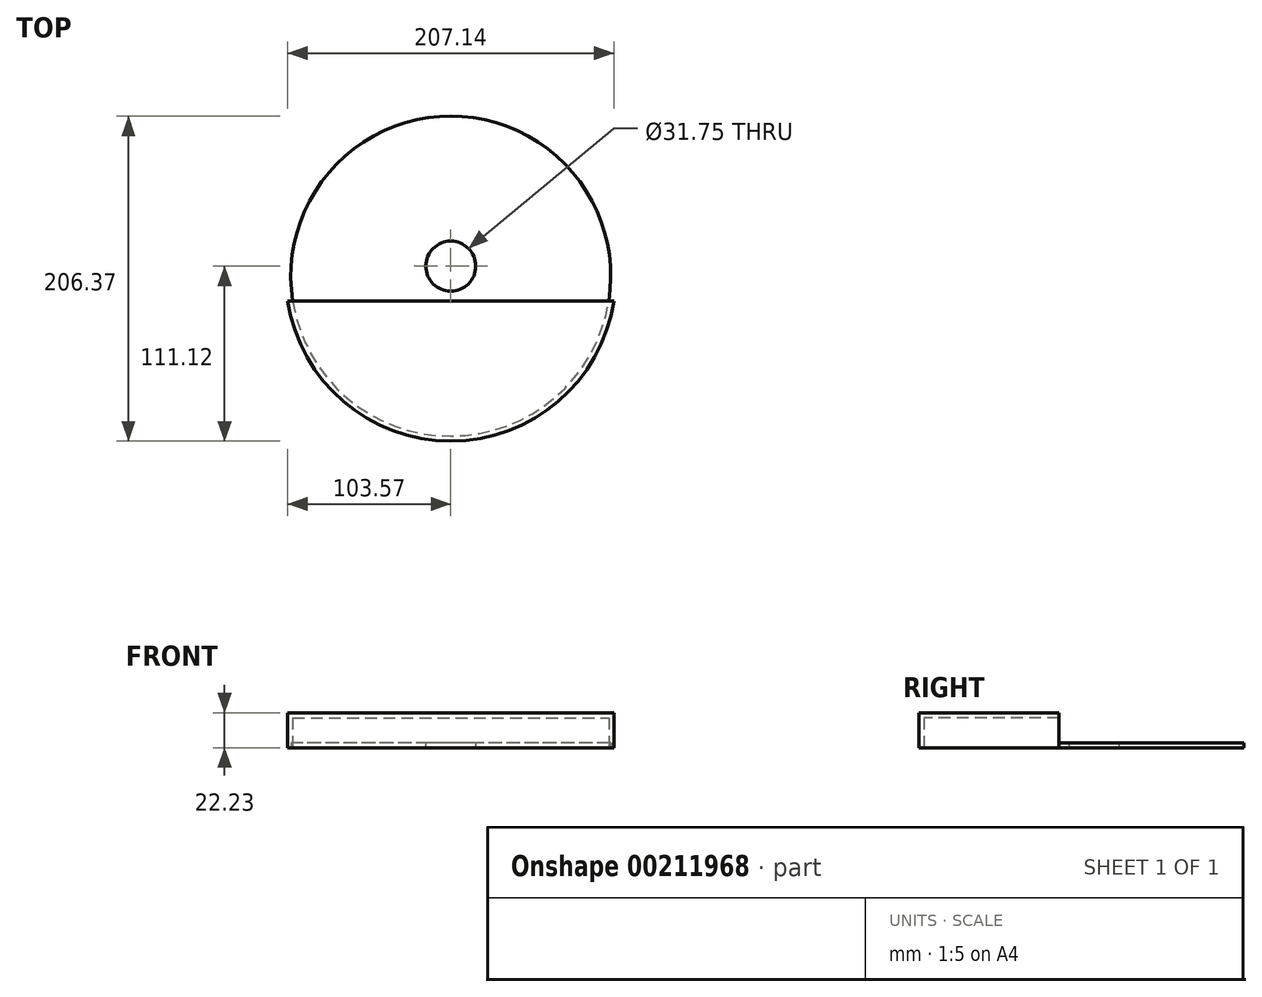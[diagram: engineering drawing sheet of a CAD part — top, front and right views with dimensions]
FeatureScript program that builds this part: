
annotation { "Feature Type Name" : "Feature", "Feature Type Description" : "" }
export const myFeature = defineFeature(function(context is Context, id is Id, definition is map)
    precondition{}
    {
        {
            var Q0;
            Q0=qCreatedBy(makeId("Top.planeOp"),FACE);
            var sketch = newSketch(context, id + "F0", { "sketchPlane" : qUnion([Q0])});
            skCircle(sketch, "E0", {"center": v(0, 0) * mm, "radius": 104.78 * mm});
            skCircle(sketch, "E1", {"center": v(0, 6.35) * mm, "radius": 15.88 * mm});
            skLineSegment(sketch, "E2", {"start": v(103.57, -15.87) * mm, "end": v(-103.57, -15.88) * mm});
            skCircle(sketch, "E3", {"center": v(0, 0) * mm, "radius": 101.6 * mm});
            skSolve(sketch);
        }
        {
            var Q0;
            Q0=makeQuery(id+"F0.imprint","IMPRINT",FACE,{"disambiguationData":[TD([[makeQuery(id+"F0.imprint","IMPRINT",EDGE,{"derivedFrom":sQuery(id+"F0.wireOp",EDGE,"E1")}),-1.0]])]});
            extrude(context, id + "F1", {"entities" : qUnion([Q0]), "depth" : 3.17 * mm});
        }
        {
            var Q0;
            {var subQ0=sQuery(id+"F0.wireOp",EDGE,"E2");var subQ1=sQuery(id+"F0.wireOp",EDGE,"E0");var subQ2=makeQuery(id+"F0.imprint","INTERSECT",VERTEX,{"disambiguationData":[OD(0.0)],"derivedFrom":[subQ1,subQ0]});Q0=makeQuery(id+"F0.imprint","IMPRINT",FACE,{"disambiguationData":[TD([[makeQuery(id+"F0.imprint","IMPRINT",EDGE,{"disambiguationData":[TD([[subQ2,-1.0]])],"derivedFrom":subQ1}),1.0]])]});}
            extrude(context, id + "F2", {"entities" : qUnion([Q0]), "operationType" : NewBodyOperationType.ADD, "depth" : 19.05 * mm});
        }
        {
            var Q0;
            Q0=makeQuery(id+"F2.opExtrude","CAP_FACE",FACE,{"disambiguationData":[OSD([sQuery(id+"F0.wireOp",EDGE,"E0"),sQuery(id+"F0.wireOp",EDGE,"E2"),sQuery(id+"F0.wireOp",EDGE,"E3")])],"isStart":false});
            var sketch = newSketch(context, id + "F3", { "sketchPlane" : qUnion([Q0])});
            skCircle(sketch, "E4", {"center": v(0, 0) * mm, "radius": 104.78 * mm});
            skLineSegment(sketch, "E5", {"start": v(-103.57, -15.88) * mm, "end": v(103.57, -15.87) * mm});
            skCircle(sketch, "E6", {"center": v(0, 6.35) * mm, "radius": 15.88 * mm});
            skSolve(sketch);
        }
        {
            var Q0;
            {var subQ1=makeQuery(id+"F2.opExtrude","CAP_EDGE",EDGE,{"disambiguationData":[OSD([sQuery(id+"F0.wireOp",EDGE,"E3")])],"isStart":false});Q0=makeQuery(id+"F3.imprint","IMPRINT",FACE,{"disambiguationData":[TD([[makeQuery(id+"F3.imprint","IMPRINT",EDGE,{"derivedFrom":subQ1}),1.0]])]});}
            var Q1;
            {var subQ4=makeQuery(id+"F2.opExtrude","CAP_EDGE",EDGE,{"disambiguationData":[OSD([sQuery(id+"F0.wireOp",EDGE,"E3")])],"isStart":false});Q1=makeQuery(id+"F3.imprint","IMPRINT",FACE,{"disambiguationData":[TD([[makeQuery(id+"F3.imprint","IMPRINT",EDGE,{"derivedFrom":subQ4}),-1.0]])]});}
            extrude(context, id + "F4", {"entities" : qUnion([Q0, Q1]), "operationType" : NewBodyOperationType.ADD, "depth" : 3.17 * mm});
        }
    });
